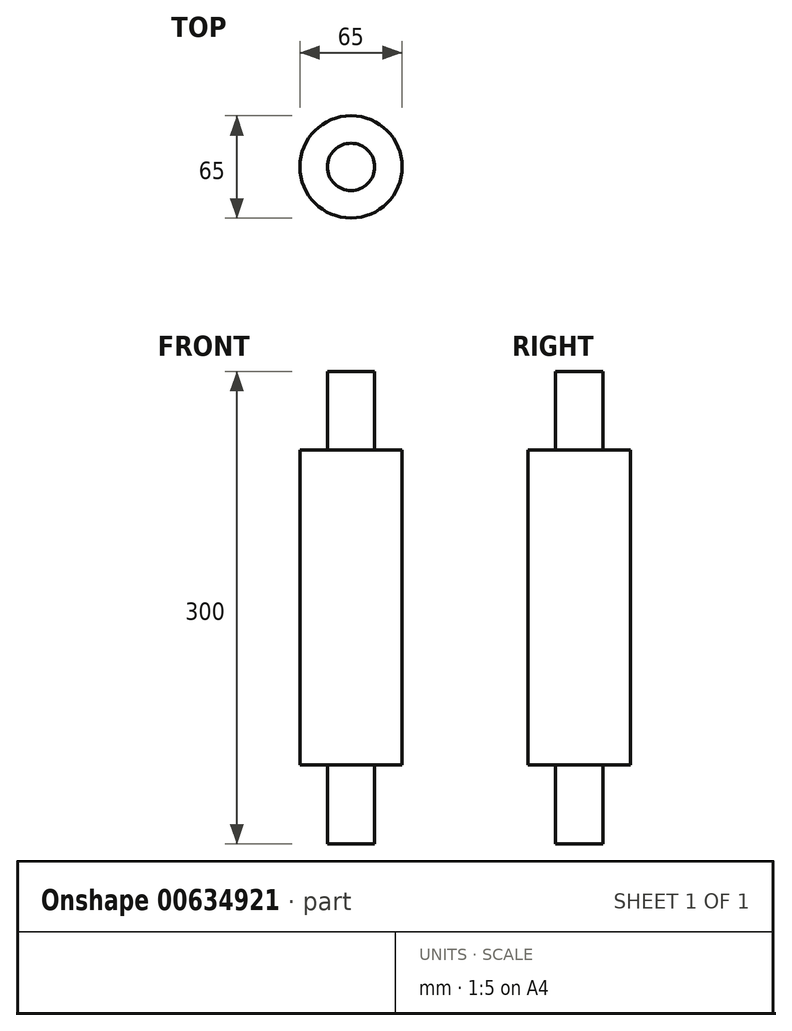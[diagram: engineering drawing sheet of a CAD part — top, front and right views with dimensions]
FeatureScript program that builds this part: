
annotation { "Feature Type Name" : "Feature", "Feature Type Description" : "" }
export const myFeature = defineFeature(function(context is Context, id is Id, definition is map)
    precondition{}
    {
        {
            var Q0;
            Q0=qCreatedBy(makeId("Top.planeOp"),FACE);
            var sketch = newSketch(context, id + "F0", { "sketchPlane" : qUnion([Q0])});
            skCircle(sketch, "E0", {"center": v(0, 0) * mm, "radius": 32.5 * mm});
            skSolve(sketch);
        }
        {
            var Q0;
            Q0 = qSketchRegion(id + "F0", true);
            extrude(context, id + "F1", {"entities" : qUnion([Q0]), "depth" : 200 * mm, "offsetDistance" : 25 * mm});
        }
        {
            var Q0;
            Q0=makeQuery(id+"F1.opExtrude","CAP_FACE",FACE,{"disambiguationData":[OSD([sQuery(id+"F0.wireOp",EDGE,"E0")])],"isStart":false});
            var sketch = newSketch(context, id + "F2", { "sketchPlane" : qUnion([Q0])});
            skCircle(sketch, "E1", {"center": v(0, 0) * mm, "radius": 15 * mm});
            skSolve(sketch);
        }
        {
            var Q0;
            Q0 = qSketchRegion(id + "F2", true);
            extrude(context, id + "F3", {"entities" : qUnion([Q0]), "operationType" : NewBodyOperationType.ADD, "depth" : 50 * mm, "offsetDistance" : 25 * mm});
        }
        {
            var Q0;
            Q0 = qSketchRegion(id + "F2", true);
            extrude(context, id + "F4", {"entities" : qUnion([Q0]), "operationType" : NewBodyOperationType.ADD, "oppositeDirection" : true, "depth" : 250 * mm, "offsetDistance" : 25 * mm});
        }
    });
